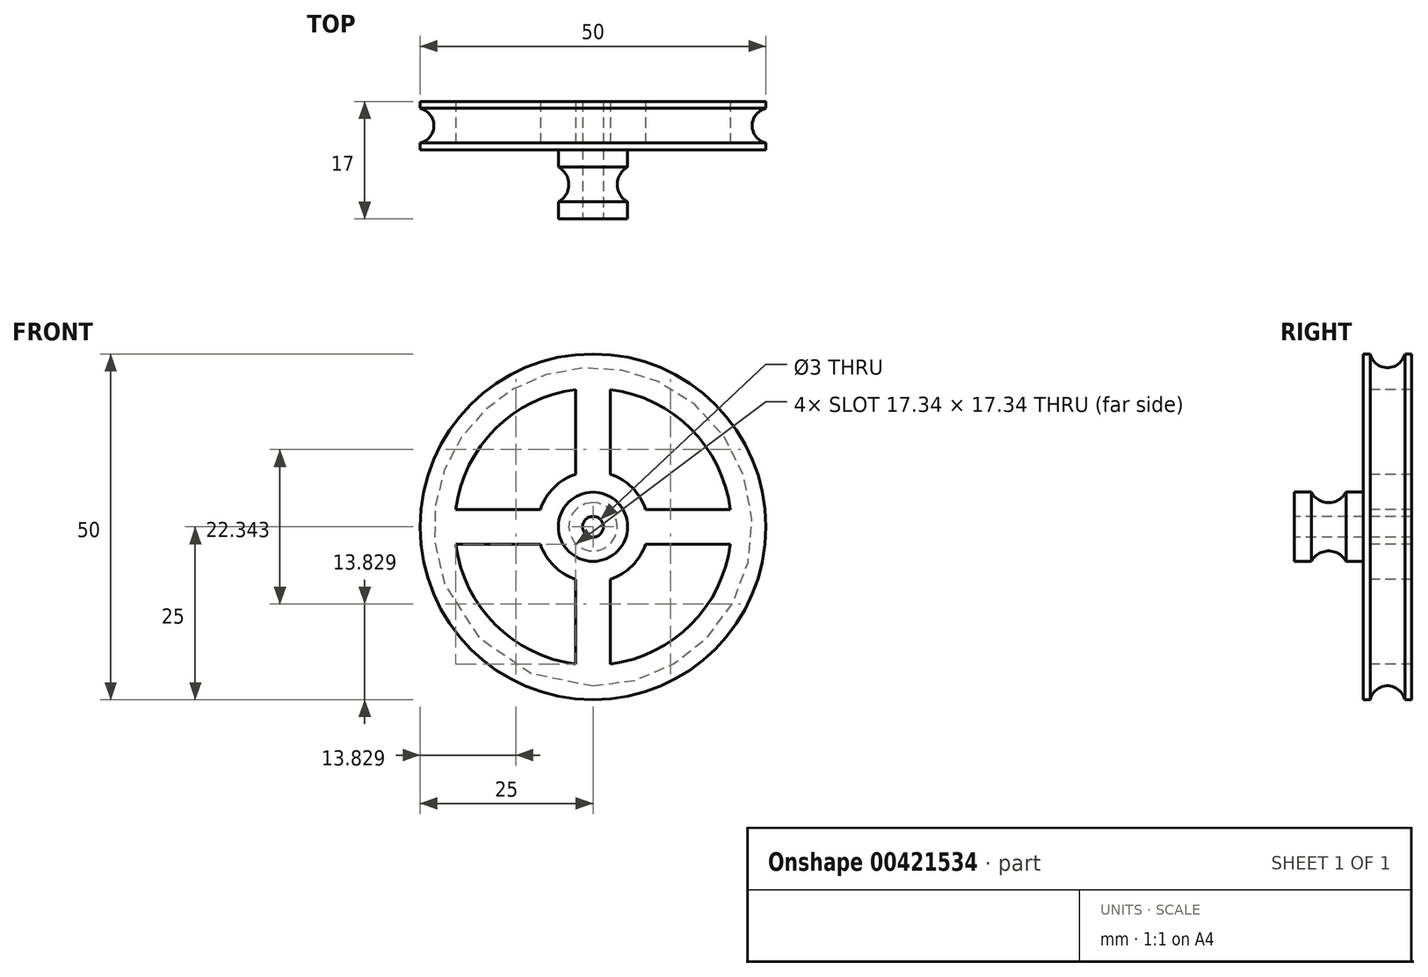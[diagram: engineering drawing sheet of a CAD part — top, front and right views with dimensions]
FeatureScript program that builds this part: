
annotation { "Feature Type Name" : "Feature", "Feature Type Description" : "" }
export const myFeature = defineFeature(function(context is Context, id is Id, definition is map)
    precondition{}
    {
        {
            var Q0;
            Q0=qCreatedBy(makeId("Front.planeOp"),FACE);
            var sketch = newSketch(context, id + "F0", { "sketchPlane" : qUnion([Q0])});
            skCircle(sketch, "E0", {"center": v(0, 0) * mm, "radius": 25 * mm});
            skSolve(sketch);
        }
        {
            var Q0;
            Q0=qSketchRegion(id+"F0",true);
            extrude(context, id + "F1", {"entities" : qUnion([Q0]), "depth" : 7 * mm});
        }
        {
            var Q0;
            Q0=qCreatedBy(makeId("Right.planeOp"),FACE);
            var sketch = newSketch(context, id + "F2", { "sketchPlane" : qUnion([Q0])});
            skPoint(sketch, "E1.middle", {"position": v(-3.5, -7.5) * mm});
            skLineSegment(sketch, "E2.bottom", {"start": v(-7, 25) * mm, "end": v(0, 25) * mm, "construction": true});
            skLineSegment(sketch, "E2.top", {"start": v(-7, -25) * mm, "end": v(0, -25) * mm, "construction": true});
            skLineSegment(sketch, "E2.left", {"start": v(-7, 25) * mm, "end": v(-7, -25) * mm, "construction": true});
            skLineSegment(sketch, "E2.right", {"start": v(0, 25) * mm, "end": v(0, -25) * mm, "construction": true});
            skPoint(sketch, "E2.middle", {"position": v(-3.5, 0) * mm});
            skArc(sketch, "E3", {"start": v(-6, 25) * mm, "mid": v(-3.5, 23) * mm, "end": v(-1, 25) * mm});
            skPoint(sketch, "E3.centerSnap0", {"position": v(-3.5, 25) * mm});
            skLineSegment(sketch, "E4", {"start": v(-6, 25) * mm, "end": v(-1, 25) * mm});
            skSolve(sketch);
        }
        {
            var Q0;
            Q0=qCreatedBy(makeId("Right.planeOp"),FACE);
            var sketch = newSketch(context, id + "F3", { "sketchPlane" : qUnion([Q0])});
            skLineSegment(sketch, "E5", {"start": v(0, 0) * mm, "end": v(-16.35, 0) * mm});
            skSolve(sketch);
        }
        {
            var Q0;
            Q0=qSketchRegion(id+"F2",true);
            var Q1;
            Q1=sQuery(id+"F3.wireOp",EDGE,"E5");
            revolve(context, id + "F4", {"operationType" : NewBodyOperationType.REMOVE, "entities" : qUnion([Q0]), "axis" : qUnion([Q1]), "revolveType" : RevolveType.FULL, "oppositeDirection" : true});
        }
        {
            var Q0;
            Q0=makeQuery(id+"F1.opExtrude","CAP_FACE",FACE,{"disambiguationData":[OSD([sQuery(id+"F0.wireOp",EDGE,"E0")])],"isStart":false});
            var sketch = newSketch(context, id + "F5", { "sketchPlane" : qUnion([Q0])});
            skCircle(sketch, "E6", {"center": v(0, 0) * mm, "radius": 5 * mm});
            skSolve(sketch);
        }
        {
            var Q0;
            Q0 = qSketchRegion(id + "F5", true);
            extrude(context, id + "F6", {"entities" : qUnion([Q0]), "operationType" : NewBodyOperationType.ADD, "depth" : 10 * mm});
        }
        {
            var Q0;
            Q0=qCreatedBy(makeId("Top.planeOp"),FACE);
            var sketch = newSketch(context, id + "F7", { "sketchPlane" : qUnion([Q0])});
            skLineSegment(sketch, "E7", {"start": v(0, -18.46) * mm, "end": v(0, -4.1) * mm});
            skSolve(sketch);
        }
        {
            var Q0;
            Q0=qCreatedBy(makeId("Right.planeOp"),FACE);
            var sketch = newSketch(context, id + "F8", { "sketchPlane" : qUnion([Q0])});
            skLineSegment(sketch, "E8.bottom", {"start": v(-17, 5) * mm, "end": v(-7, 5) * mm, "construction": true});
            skLineSegment(sketch, "E8.top", {"start": v(-17, -5) * mm, "end": v(-7, -5) * mm, "construction": true});
            skLineSegment(sketch, "E8.left", {"start": v(-17, 5) * mm, "end": v(-17, -5) * mm, "construction": true});
            skLineSegment(sketch, "E8.right", {"start": v(-7, 5) * mm, "end": v(-7, -5) * mm, "construction": true});
            skPoint(sketch, "E8.middle", {"position": v(-12, 0) * mm});
            skArc(sketch, "E9", {"start": v(-9.5, 5) * mm, "mid": v(-12, 3.5) * mm, "end": v(-14.5, 5) * mm});
            skLineSegment(sketch, "E10", {"start": v(-9.5, 5) * mm, "end": v(-14.5, 5) * mm});
            skSolve(sketch);
        }
        {
            var Q0;
            Q0 = qSketchRegion(id + "F8", true);
            var Q1;
            Q1=sQuery(id+"F7.wireOp",EDGE,"E7");
            revolve(context, id + "F9", {"operationType" : NewBodyOperationType.REMOVE, "entities" : qUnion([Q0]), "axis" : qUnion([Q1]), "revolveType" : RevolveType.FULL, "oppositeDirection" : true});
        }
        {
            var Q0;
            Q0=makeQuery(id+"F6.opExtrude","CAP_FACE",FACE,{"disambiguationData":[OSD([sQuery(id+"F5.wireOp",EDGE,"E6")])],"isStart":false});
            var sketch = newSketch(context, id + "F10", { "sketchPlane" : qUnion([Q0])});
            skCircle(sketch, "E11", {"center": v(0, 0) * mm, "radius": 1.5 * mm});
            skSolve(sketch);
        }
        {
            var Q0;
            Q0 = qSketchRegion(id + "F10", true);
            extrude(context, id + "F11", {"entities" : qUnion([Q0]), "operationType" : NewBodyOperationType.REMOVE, "endBound" : BoundingType.THROUGH_ALL, "oppositeDirection" : true, "depth" : 25 * mm});
        }
        {
            var Q0;
            Q0=makeQuery(id+"F1.opExtrude","CAP_FACE",FACE,{"disambiguationData":[OSD([sQuery(id+"F0.wireOp",EDGE,"E0")])],"isStart":false});
            var sketch = newSketch(context, id + "F12", { "sketchPlane" : qUnion([Q0])});
            skArc(sketch, "E12", {"start": v(-2.5, 19.84) * mm, "mid": v(-14.14, 14.14) * mm, "end": v(-19.84, 2.5) * mm});
            skArc(sketch, "E13", {"start": v(-2.5, 7.6) * mm, "mid": v(-5.66, 5.66) * mm, "end": v(-7.6, 2.5) * mm});
            skLineSegment(sketch, "E14", {"start": v(-19.84, 2.5) * mm, "end": v(-7.6, 2.5) * mm});
            skLineSegment(sketch, "E15", {"start": v(-2.5, 7.6) * mm, "end": v(-2.5, 19.84) * mm});
            skLineSegment(sketch, "E16.MirrorCS", {"start": v(19.84, 2.5) * mm, "end": v(7.6, 2.5) * mm});
            skLineSegment(sketch, "E17.MirrorCS", {"start": v(2.5, 7.6) * mm, "end": v(2.5, 19.84) * mm});
            skArc(sketch, "E18.MirrorCS", {"start": v(2.5, 7.6) * mm, "mid": v(5.66, 5.66) * mm, "end": v(7.6, 2.5) * mm});
            skArc(sketch, "E19.MirrorCS", {"start": v(2.5, 19.84) * mm, "mid": v(14.14, 14.14) * mm, "end": v(19.84, 2.5) * mm});
            skLineSegment(sketch, "E20.MirrorCS", {"start": v(19.84, -2.5) * mm, "end": v(7.6, -2.5) * mm});
            skArc(sketch, "E21.MirrorCS", {"start": v(2.5, -19.84) * mm, "mid": v(14.14, -14.14) * mm, "end": v(19.84, -2.5) * mm});
            skLineSegment(sketch, "E22.MirrorCS", {"start": v(2.5, -7.6) * mm, "end": v(2.5, -19.84) * mm});
            skArc(sketch, "E23.MirrorCS", {"start": v(2.5, -7.6) * mm, "mid": v(5.66, -5.66) * mm, "end": v(7.6, -2.5) * mm});
            skLineSegment(sketch, "E24.MirrorCS", {"start": v(-2.5, -7.6) * mm, "end": v(-2.5, -19.84) * mm});
            skLineSegment(sketch, "E25.MirrorCS", {"start": v(-19.84, -2.5) * mm, "end": v(-7.6, -2.5) * mm});
            skArc(sketch, "E26.MirrorCS", {"start": v(-2.5, -7.6) * mm, "mid": v(-5.66, -5.66) * mm, "end": v(-7.6, -2.5) * mm});
            skArc(sketch, "E27.MirrorCS", {"start": v(-2.5, -19.84) * mm, "mid": v(-14.14, -14.14) * mm, "end": v(-19.84, -2.5) * mm});
            skSolve(sketch);
        }
        {
            var Q0;
            Q0 = qSketchRegion(id + "F12", true);
            extrude(context, id + "F13", {"entities" : qUnion([Q0]), "operationType" : NewBodyOperationType.REMOVE, "endBound" : BoundingType.THROUGH_ALL, "oppositeDirection" : true, "depth" : 25 * mm});
        }
    });
